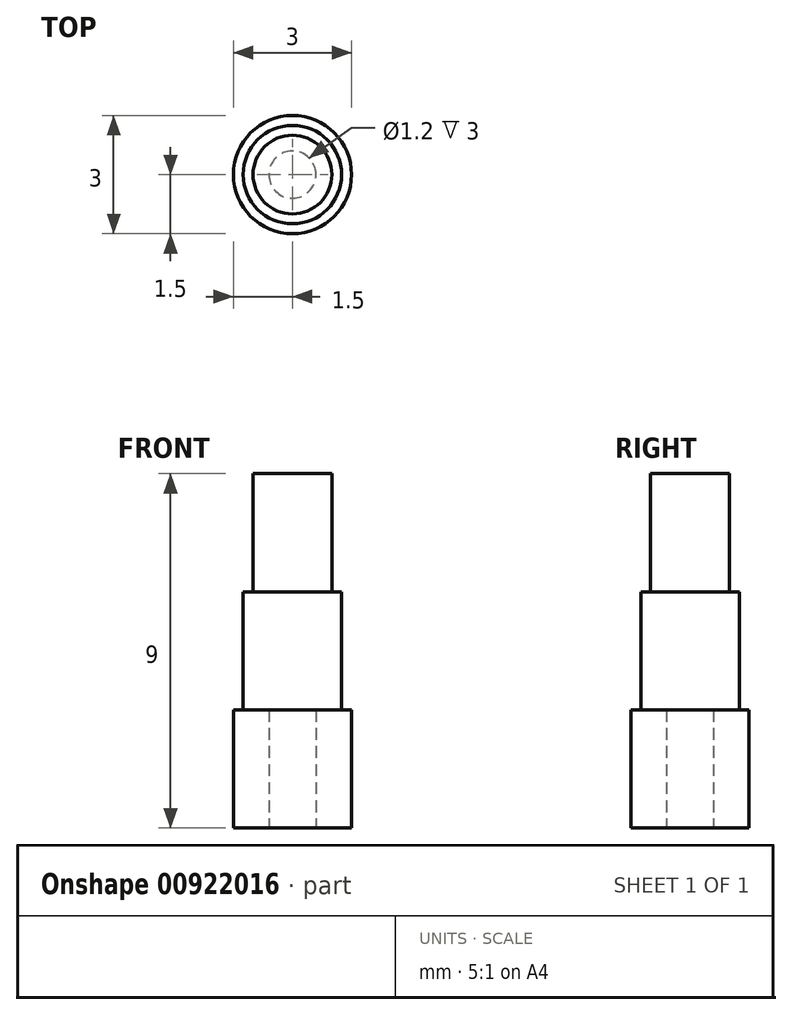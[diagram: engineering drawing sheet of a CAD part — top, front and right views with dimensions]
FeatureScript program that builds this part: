
annotation { "Feature Type Name" : "Feature", "Feature Type Description" : "" }
export const myFeature = defineFeature(function(context is Context, id is Id, definition is map)
    precondition{}
    {
        {
            var Q0;
            Q0=qCreatedBy(makeId("Top.planeOp"),FACE);
            var sketch = newSketch(context, id + "F0", { "sketchPlane" : qUnion([Q0])});
            skCircle(sketch, "E0", {"center": v(0, 0) * mm, "radius": 1 * mm});
            skSolve(sketch);
        }
        {
            var Q0;
            Q0=qCreatedBy(makeId("Top.planeOp"),FACE);
            var sketch = newSketch(context, id + "F1", { "sketchPlane" : qUnion([Q0])});
            skCircle(sketch, "E1", {"center": v(0, 0) * mm, "radius": 1.25 * mm});
            skSolve(sketch);
        }
        {
            var Q0;
            Q0=qSketchRegion(id+"F1",true);
            extrude(context, id + "F2", {"entities" : qUnion([Q0]), "depth" : 6 * mm, "offsetDistance" : 25 * mm});
        }
        {
            var Q0;
            Q0=qSketchRegion(id+"F0",true);
            extrude(context, id + "F3", {"entities" : qUnion([Q0]), "operationType" : NewBodyOperationType.ADD, "depth" : 9 * mm, "offsetDistance" : 25 * mm});
        }
        {
            var Q0;
            Q0=qCreatedBy(makeId("Top.planeOp"),FACE);
            var sketch = newSketch(context, id + "F4", { "sketchPlane" : qUnion([Q0])});
            skCircle(sketch, "E2", {"center": v(0, 0) * mm, "radius": 1.5 * mm});
            skSolve(sketch);
        }
        {
            var Q0;
            Q0 = qSketchRegion(id + "F4", true);
            extrude(context, id + "F5", {"entities" : qUnion([Q0]), "operationType" : NewBodyOperationType.ADD, "depth" : 3 * mm, "offsetDistance" : 25 * mm});
        }
        {
            var Q0;
            Q0=qCreatedBy(makeId("Top.planeOp"),FACE);
            var sketch = newSketch(context, id + "F6", { "sketchPlane" : qUnion([Q0])});
            skCircle(sketch, "E3", {"center": v(0, 0) * mm, "radius": 0.6 * mm});
            skSolve(sketch);
        }
        {
            var Q0;
            Q0 = qSketchRegion(id + "F6", true);
            extrude(context, id + "F7", {"entities" : qUnion([Q0]), "operationType" : NewBodyOperationType.REMOVE, "depth" : 3 * mm, "offsetDistance" : 25 * mm});
        }
    });
